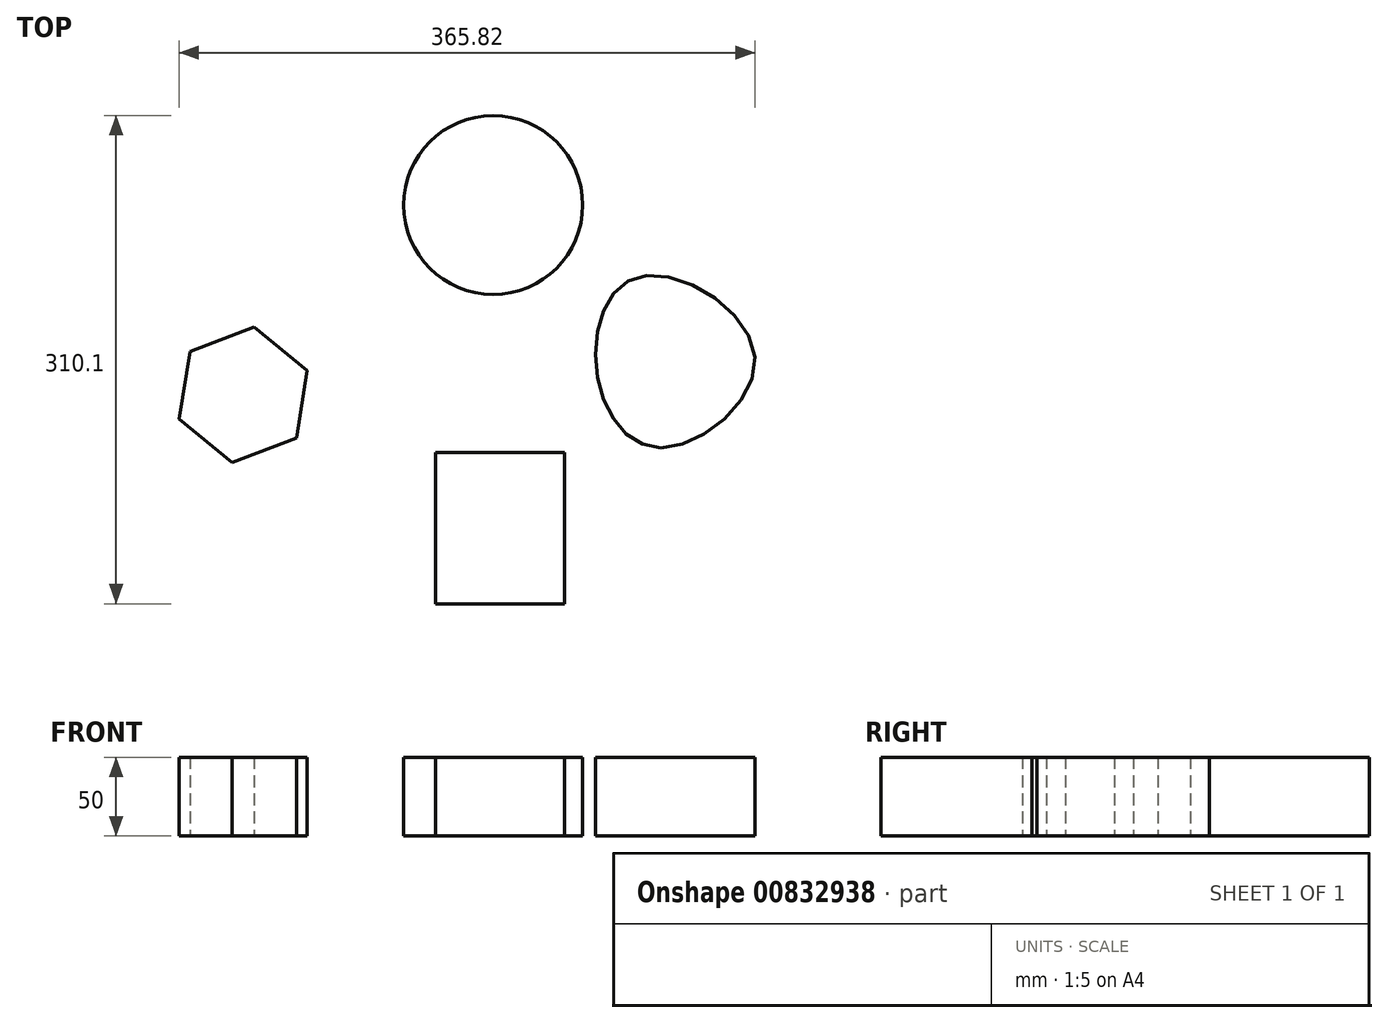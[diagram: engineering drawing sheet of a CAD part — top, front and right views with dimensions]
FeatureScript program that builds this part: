
annotation { "Feature Type Name" : "Feature", "Feature Type Description" : "" }
export const myFeature = defineFeature(function(context is Context, id is Id, definition is map)
    precondition{}
    {
        {
            var Q0;
            Q0=qCreatedBy(makeId("Top.planeOp"),FACE);
            var sketch = newSketch(context, id + "F0", { "sketchPlane" : qUnion([Q0])});
            skCircle(sketch, "E0.cCircle", {"center": v(-144, 0) * mm, "radius": 37.75 * mm, "construction": true});
            skLineSegment(sketch, "E0.0", {"start": v(-177.8, 27.52) * mm, "end": v(-137.06, 43.03) * mm});
            skLineSegment(sketch, "E0.1", {"start": v(-137.06, 43.03) * mm, "end": v(-103.26, 15.5) * mm});
            skLineSegment(sketch, "E0.2", {"start": v(-103.26, 15.5) * mm, "end": v(-110.2, -27.52) * mm});
            skLineSegment(sketch, "E0.3", {"start": v(-110.2, -27.52) * mm, "end": v(-150.93, -43.03) * mm});
            skLineSegment(sketch, "E0.4", {"start": v(-150.93, -43.03) * mm, "end": v(-184.73, -15.5) * mm});
            skLineSegment(sketch, "E0.5", {"start": v(-184.73, -15.5) * mm, "end": v(-177.8, 27.52) * mm});
            skPoint(sketch, "E0.0.midPoint", {"position": v(-157.42, 35.28) * mm});
            skCircle(sketch, "E1", {"center": v(14.78, 120.51) * mm, "radius": 56.85 * mm});
            skLineSegment(sketch, "E2.bottom", {"start": v(-21.91, -132.74) * mm, "end": v(60, -132.74) * mm});
            skLineSegment(sketch, "E2.top", {"start": v(-21.91, -36.8) * mm, "end": v(60, -36.8) * mm});
            skLineSegment(sketch, "E2.left", {"start": v(-21.91, -132.74) * mm, "end": v(-21.91, -36.8) * mm});
            skLineSegment(sketch, "E2.right", {"start": v(60, -132.74) * mm, "end": v(60, -36.8) * mm});
            skFitSpline(sketch, "E3", {"points": [v(121.55, -33.7) * mm, v(80.46, 15.54) * mm, v(108.33, 75.21) * mm, v(180.94, 24.92) * mm, v(121.55, -33.7) * mm]});
            skSolve(sketch);
        }
        {
            var Q0;
            Q0=makeQuery(id+"F0.imprint","IMPRINT",FACE,{"disambiguationData":[TD([[makeQuery(id+"F0.imprint","IMPRINT",EDGE,{"derivedFrom":sQuery(id+"F0.wireOp",EDGE,"E2.bottom")}),1.0]])]});
            var Q1;
            Q1=makeQuery(id+"F0.imprint","IMPRINT",FACE,{"disambiguationData":[TD([[makeQuery(id+"F0.imprint","IMPRINT",EDGE,{"derivedFrom":sQuery(id+"F0.wireOp",EDGE,"E0.0")}),-1.0]])]});
            var Q2;
            Q2=makeQuery(id+"F0.imprint","IMPRINT",FACE,{"disambiguationData":[TD([[makeQuery(id+"F0.imprint","IMPRINT",EDGE,{"derivedFrom":sQuery(id+"F0.wireOp",EDGE,"E1")}),1.0]])]});
            var Q3;
            Q3=makeQuery(id+"F0.imprint","IMPRINT",FACE,{"disambiguationData":[TD([[makeQuery(id+"F0.imprint","IMPRINT",EDGE,{"derivedFrom":sQuery(id+"F0.wireOp",EDGE,"E3")}),-1.0]])]});
            extrude(context, id + "F1", {"entities" : qUnion([Q0, Q1, Q2, Q3]), "depth" : 50 * mm, "offsetDistance" : 25 * mm});
        }
    });
